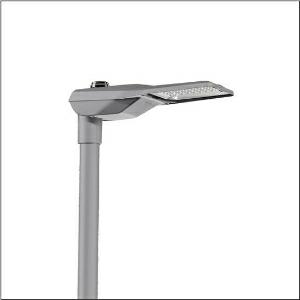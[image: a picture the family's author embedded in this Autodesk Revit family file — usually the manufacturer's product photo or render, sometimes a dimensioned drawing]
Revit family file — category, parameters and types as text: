
# Revit family: streetlight_sl_21_mini___st1_0a_5xe6d37n08gb_0daf
name_source: partatom
category: Lighting Fixtures
units: mm (PartAtom-declared; Revit-internal decimal feet)

## family parameters
Cut with Voids When Loaded = No
Host = Face
Light Source = No
Part Type = Normal
Room Calculation Point = No
Round Connector Dimension = Use Diameter
Shared = No

## types (1)
- --- (1 x LED, 5940 lm, 40.4 W, 3000K)
    Apparent Load = 40 VA
    CIE Flux Codes = 37 72 97 100 100
    Color Rendering = 70
    Color Temperature = 3000K
    Default Elevation = 1800 mm
    Description = Streetlight SL 21 mini, mast luminaire, primary light control with lens, of PMMA, primary optical cover: cover, of toughened safety glass, transparent, light distribution: ST1.0a, light emission: direct distribution, primary light characteristic: asymmetric, installation type: side-entry, LED, 3G 1.5mm², High Power LED, rated luminous flux: 5.940lm, luminous efficacy: 147lm/W, light colour: 730, colour temperature: 3000K, control gear: NEMA (7pin), control: overheat protection, pre-setting: linear dimming characteristic, constant luminous flux control, time-dependent luminous flux control, flexible luminous flux parameterisation, mains connection: 230..240V, AC, 50/60Hz, connection cable pre-assembled, cable length: 8,5m, wiring characteristics: H07RN-F, start of lifetime: 40W, end of service life: 41W, reduction: 19W, luminaire housing, of diecast aluminium (EN AC-44300), powder-coated, Siteco® metallic grey (DB 702S), corrosivity category C5 mid according to DIN EN ISO 12944, multi-level sealing system, sealing non-destructively replaceable, inclination adjustable: 0°, 5°, 10°, 15°, length: 628mm, width: 235mm, height: 110mm, spigot size: 42mm (side-entry), mounting height: 4..8m, protection rating (complete): IP66, insulation class (complete): insulation class I (protective earthing), certification: CE, ENEC, ENEC+, VDE, impact resistance: IK10, permissible operating ambient temperature for outdoor applications: -40..+50°C, standard-compliant lighting for roads and squares, packaging unit: 1 piece

Light Distribution: ST1.0a
    Height = 110 mm
    Lamp = 1 x LED
    Lamp Light Flux = 5940 lm
    Lamp Power = 40.4 W
    Lamp count = 1
    Length = 625 mm
    Luminous efficacy = 147 lm/W
    Manufacturer = Siteco
    ModVariant = No
    Model = 5XE6D37N08GB
    Number of Poles = 1
    OnlyDefault = Yes
    Power Factor = 1
    Product Name = Streetlight SL 21 mini | ST1.0a
    Product group = mast luminaire | pylon top
    ProductGroupID = 6100
    Protection Class = Protection class I
    Protection Degree = IP 66
    RLX_Detail_Level = 1
    RLX_Emergency_Light_Flux = 0 lm
    RLX_Emergency_Type = 0
    RLX_Emergency_Type_DB = No
    RlxData = <blob elided: 25773 chars, md5=8086be28>
    Socket = socket
    Standby Power = 0 W
    System Light Flux = 5940 lm
    System Power = 40 W
    Type Comments = factory setting: luminous flux: 100 % | dim-lin: 254 | 812 mA
    Type Image = l_1294379.jpg
    URL = http://relux.com
    VarID = @adj_136322
    Voltage = 0 V
    Weight = 0.00 kg
    Width = 234 mm

## geometry (parser evidence)
native form markers: Blend x4, Sweep x10
no freeform markers — native parametric forms only
